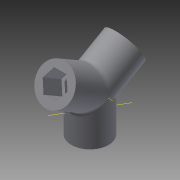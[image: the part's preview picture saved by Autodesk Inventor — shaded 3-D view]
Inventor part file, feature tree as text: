
AUTODESK INVENTOR PART (.ipt)
format: ipt  version: 2015 SP1 (Build 190203100, 203)  size: 213,504 bytes
history: native  units: mm
features: extrude x5, sketch x5, other x4, projected_geometry x3, pattern_circular x1, fillet x1
ambient origin geometry x8: Origin, YZ Plane, XZ Plane, XY Plane, X Axis, Y Axis, Z Axis, Center Point
bodies: Body1 (feature_tree)
feature tree (19):
  other  "Sólido1"
  extrude  "Extrusión1"  Depth=12.0mm
  extrude  "Extrusión2"  Depth=6.0mm TaperAngle=0.0deg
  other  "Eje de trabajo1"
  other  "Eje de trabajo2"
  pattern_circular  "Patrón circular3"  Count=3 Angle=360.0deg
  extrude  "Extrusión8"  Depth=6.0mm TaperAngle=0.0deg
  extrude  "Extrusión9"  Depth=2.0mm
  extrude  "Extrusión10"  [1 undecoded]
  fillet  "Empalme3"  [1 undecoded]
  sketch  "Boceto1"  dims[d0=8.0mm d1=12.0mm]
  sketch  "Boceto2"  dims[d2=7.0mm d3=0.0mm d4=6.0mm d5=0.0mm d19=30.0mm d20=360.0deg]
  other  "Punto de trabajo1"
  sketch  "Boceto9"  dims[d27=6.0mm d28=0.0mm d29=6.0mm d30=0.0mm]
  projected_geometry  "Contorno proyectado7"
  sketch  "Boceto10"  dims[d31=6.0mm d32=0.0mm d33=2.0mm]
  projected_geometry  "Contorno proyectado8"
  sketch  "Boceto11"
  projected_geometry  "Contorno proyectado9"
note: 2 required parameter values undecoded (feature->parameter linkage not recoverable at this tier; creation-order binding heuristic only, values carry confidence <= 0.55)
